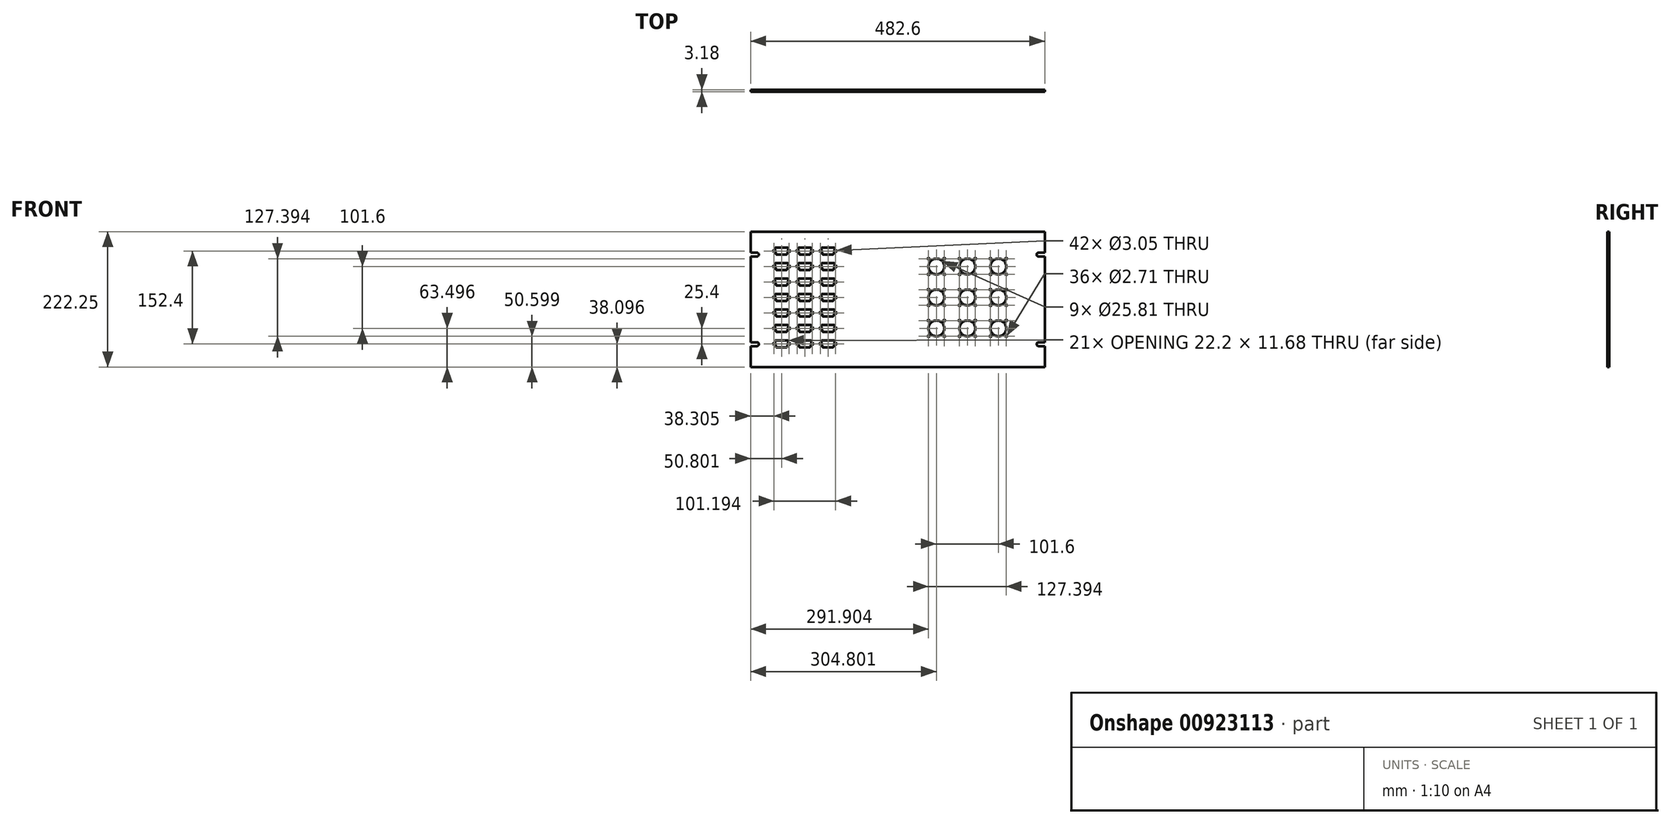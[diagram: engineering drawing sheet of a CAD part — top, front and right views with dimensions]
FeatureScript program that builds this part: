
annotation { "Feature Type Name" : "Feature", "Feature Type Description" : "" }
export const myFeature = defineFeature(function(context is Context, id is Id, definition is map)
    precondition{}
    {
        {
            var Q0;
            Q0=qCreatedBy(makeId("Front.planeOp"),FACE);
            var sketch = newSketch(context, id + "F0", { "sketchPlane" : qUnion([Q0])});
            skLineSegment(sketch, "E0.bottom", {"start": v(-256.05, -169.36) * mm, "end": v(226.55, -169.36) * mm});
            skLineSegment(sketch, "E0.top", {"start": v(-256.05, 52.89) * mm, "end": v(226.55, 52.89) * mm});
            skLineSegment(sketch, "E0.left", {"start": v(-256.05, -169.36) * mm, "end": v(-256.05, -134.95) * mm});
            skLineSegment(sketch, "E0.right", {"start": v(226.55, -169.36) * mm, "end": v(226.55, -134.95) * mm});
            skCircle(sketch, "E1", {"center": v(-217.75, -131.26) * mm, "radius": 1.52 * mm});
            skCircle(sketch, "E2", {"center": v(-192.75, -131.26) * mm, "radius": 1.52 * mm});
            skLineSegment(sketch, "E3", {"start": v(-217.75, -131.26) * mm, "end": v(-192.75, -131.26) * mm, "construction": true});
            skLineSegment(sketch, "E4", {"start": v(-205.25, -137.1) * mm, "end": v(-205.25, -125.42) * mm, "construction": true});
            skPoint(sketch, "E4.startSnap0", {"position": v(-205.25, -131.26) * mm});
            skLineSegment(sketch, "E5", {"start": v(-214.24, -125.42) * mm, "end": v(-196.26, -125.42) * mm});
            skLineSegment(sketch, "E6", {"start": v(-212.65, -137.1) * mm, "end": v(-197.84, -137.1) * mm});
            skLineSegment(sketch, "E7", {"start": v(-205.25, -125.42) * mm, "end": v(-205.25, -125.42) * mm});
            skLineSegment(sketch, "E8", {"start": v(-205.25, -137.1) * mm, "end": v(-205.25, -137.1) * mm});
            skArc(sketch, "E9", {"start": v(-214.24, -125.42) * mm, "mid": v(-215.88, -126.2) * mm, "end": v(-216.3, -127.97) * mm});
            skArc(sketch, "E10", {"start": v(-194.2, -127.97) * mm, "mid": v(-194.62, -126.2) * mm, "end": v(-196.26, -125.42) * mm});
            skArc(sketch, "E11", {"start": v(-197.84, -137.1) * mm, "mid": v(-196.52, -136.64) * mm, "end": v(-195.78, -135.44) * mm});
            skArc(sketch, "E12", {"start": v(-214.71, -135.44) * mm, "mid": v(-213.98, -136.64) * mm, "end": v(-212.65, -137.1) * mm});
            skPoint(sketch, "E13.orphan", {"position": v(-115.92, -125.42) * mm});
            skPoint(sketch, "E14.orphan", {"position": v(-123.87, -137.1) * mm});
            skLineSegment(sketch, "E15", {"start": v(-216.3, -127.97) * mm, "end": v(-214.71, -135.44) * mm});
            skLineSegment(sketch, "E16", {"start": v(-194.2, -127.97) * mm, "end": v(-195.78, -135.44) * mm});
            skPoint(sketch, "E17.0.1.0", {"position": v(-123.87, -111.7) * mm});
            skLineSegment(sketch, "E17.0.1.1", {"start": v(-216.3, -102.57) * mm, "end": v(-214.71, -110.04) * mm});
            skLineSegment(sketch, "E17.0.1.2", {"start": v(-194.2, -102.57) * mm, "end": v(-195.78, -110.04) * mm});
            skCircle(sketch, "E17.0.1.3", {"center": v(-192.75, -105.86) * mm, "radius": 1.52 * mm});
            skLineSegment(sketch, "E17.0.1.4", {"start": v(-214.24, -100.02) * mm, "end": v(-196.26, -100.02) * mm});
            skPoint(sketch, "E17.0.1.5", {"position": v(-205.25, -105.86) * mm});
            skPoint(sketch, "E17.0.1.6", {"position": v(-115.92, -100.02) * mm});
            skLineSegment(sketch, "E17.0.1.8", {"start": v(-212.65, -111.7) * mm, "end": v(-197.84, -111.7) * mm});
            skLineSegment(sketch, "E17.0.1.9", {"start": v(-217.75, -105.86) * mm, "end": v(-192.75, -105.86) * mm, "construction": true});
            skLineSegment(sketch, "E17.0.1.11", {"start": v(-205.25, -111.7) * mm, "end": v(-205.25, -100.02) * mm, "construction": true});
            skCircle(sketch, "E17.0.1.12", {"center": v(-217.75, -105.86) * mm, "radius": 1.52 * mm});
            skArc(sketch, "E17.0.1.13", {"start": v(-214.71, -110.04) * mm, "mid": v(-213.98, -111.24) * mm, "end": v(-212.65, -111.7) * mm});
            skArc(sketch, "E17.0.1.14", {"start": v(-214.24, -100.02) * mm, "mid": v(-215.88, -100.8) * mm, "end": v(-216.3, -102.57) * mm});
            skArc(sketch, "E17.0.1.15", {"start": v(-194.2, -102.57) * mm, "mid": v(-194.62, -100.8) * mm, "end": v(-196.26, -100.02) * mm});
            skArc(sketch, "E17.0.1.16", {"start": v(-197.84, -111.7) * mm, "mid": v(-196.52, -111.24) * mm, "end": v(-195.78, -110.04) * mm});
            skPoint(sketch, "E17.0.2.0", {"position": v(-123.87, -86.3) * mm});
            skLineSegment(sketch, "E17.0.2.1", {"start": v(-216.3, -77.17) * mm, "end": v(-214.71, -84.64) * mm});
            skLineSegment(sketch, "E17.0.2.2", {"start": v(-194.2, -77.17) * mm, "end": v(-195.78, -84.64) * mm});
            skCircle(sketch, "E17.0.2.3", {"center": v(-192.75, -80.46) * mm, "radius": 1.52 * mm});
            skLineSegment(sketch, "E17.0.2.4", {"start": v(-214.24, -74.62) * mm, "end": v(-196.26, -74.62) * mm});
            skPoint(sketch, "E17.0.2.5", {"position": v(-205.25, -80.46) * mm});
            skPoint(sketch, "E17.0.2.6", {"position": v(-115.92, -74.62) * mm});
            skLineSegment(sketch, "E17.0.2.8", {"start": v(-212.65, -86.3) * mm, "end": v(-197.84, -86.3) * mm});
            skLineSegment(sketch, "E17.0.2.9", {"start": v(-217.75, -80.46) * mm, "end": v(-192.75, -80.46) * mm, "construction": true});
            skLineSegment(sketch, "E17.0.2.11", {"start": v(-205.25, -86.3) * mm, "end": v(-205.25, -74.62) * mm, "construction": true});
            skCircle(sketch, "E17.0.2.12", {"center": v(-217.75, -80.46) * mm, "radius": 1.52 * mm});
            skArc(sketch, "E17.0.2.13", {"start": v(-214.71, -84.64) * mm, "mid": v(-213.98, -85.84) * mm, "end": v(-212.65, -86.3) * mm});
            skArc(sketch, "E17.0.2.14", {"start": v(-214.24, -74.62) * mm, "mid": v(-215.88, -75.4) * mm, "end": v(-216.3, -77.17) * mm});
            skArc(sketch, "E17.0.2.15", {"start": v(-194.2, -77.17) * mm, "mid": v(-194.62, -75.4) * mm, "end": v(-196.26, -74.62) * mm});
            skArc(sketch, "E17.0.2.16", {"start": v(-197.84, -86.3) * mm, "mid": v(-196.52, -85.84) * mm, "end": v(-195.78, -84.64) * mm});
            skPoint(sketch, "E17.0.3.0", {"position": v(-123.87, -60.9) * mm});
            skLineSegment(sketch, "E17.0.3.1", {"start": v(-216.3, -51.77) * mm, "end": v(-214.71, -59.24) * mm});
            skLineSegment(sketch, "E17.0.3.2", {"start": v(-194.2, -51.77) * mm, "end": v(-195.78, -59.24) * mm});
            skCircle(sketch, "E17.0.3.3", {"center": v(-192.75, -55.06) * mm, "radius": 1.52 * mm});
            skLineSegment(sketch, "E17.0.3.4", {"start": v(-214.24, -49.22) * mm, "end": v(-196.26, -49.22) * mm});
            skPoint(sketch, "E17.0.3.5", {"position": v(-205.25, -55.06) * mm});
            skPoint(sketch, "E17.0.3.6", {"position": v(-115.92, -49.22) * mm});
            skLineSegment(sketch, "E17.0.3.8", {"start": v(-212.65, -60.9) * mm, "end": v(-197.84, -60.9) * mm});
            skLineSegment(sketch, "E17.0.3.9", {"start": v(-217.75, -55.06) * mm, "end": v(-192.75, -55.06) * mm, "construction": true});
            skLineSegment(sketch, "E17.0.3.11", {"start": v(-205.25, -60.9) * mm, "end": v(-205.25, -49.22) * mm, "construction": true});
            skCircle(sketch, "E17.0.3.12", {"center": v(-217.75, -55.06) * mm, "radius": 1.52 * mm});
            skArc(sketch, "E17.0.3.13", {"start": v(-214.71, -59.24) * mm, "mid": v(-213.98, -60.44) * mm, "end": v(-212.65, -60.9) * mm});
            skArc(sketch, "E17.0.3.14", {"start": v(-214.24, -49.22) * mm, "mid": v(-215.88, -50) * mm, "end": v(-216.3, -51.77) * mm});
            skArc(sketch, "E17.0.3.15", {"start": v(-194.2, -51.77) * mm, "mid": v(-194.62, -50) * mm, "end": v(-196.26, -49.22) * mm});
            skArc(sketch, "E17.0.3.16", {"start": v(-197.84, -60.9) * mm, "mid": v(-196.52, -60.44) * mm, "end": v(-195.78, -59.24) * mm});
            skPoint(sketch, "E17.0.4.0", {"position": v(-123.87, -35.5) * mm});
            skLineSegment(sketch, "E17.0.4.1", {"start": v(-216.3, -26.37) * mm, "end": v(-214.71, -33.84) * mm});
            skLineSegment(sketch, "E17.0.4.2", {"start": v(-194.2, -26.37) * mm, "end": v(-195.78, -33.84) * mm});
            skCircle(sketch, "E17.0.4.3", {"center": v(-192.75, -29.66) * mm, "radius": 1.52 * mm});
            skLineSegment(sketch, "E17.0.4.4", {"start": v(-214.24, -23.82) * mm, "end": v(-196.26, -23.82) * mm});
            skPoint(sketch, "E17.0.4.5", {"position": v(-205.25, -29.66) * mm});
            skPoint(sketch, "E17.0.4.6", {"position": v(-115.92, -23.82) * mm});
            skLineSegment(sketch, "E17.0.4.8", {"start": v(-212.65, -35.5) * mm, "end": v(-197.84, -35.5) * mm});
            skLineSegment(sketch, "E17.0.4.9", {"start": v(-217.75, -29.66) * mm, "end": v(-192.75, -29.66) * mm, "construction": true});
            skLineSegment(sketch, "E17.0.4.11", {"start": v(-205.25, -35.5) * mm, "end": v(-205.25, -23.82) * mm, "construction": true});
            skCircle(sketch, "E17.0.4.12", {"center": v(-217.75, -29.66) * mm, "radius": 1.52 * mm});
            skArc(sketch, "E17.0.4.13", {"start": v(-214.71, -33.84) * mm, "mid": v(-213.98, -35.04) * mm, "end": v(-212.65, -35.5) * mm});
            skArc(sketch, "E17.0.4.14", {"start": v(-214.24, -23.82) * mm, "mid": v(-215.88, -24.6) * mm, "end": v(-216.3, -26.37) * mm});
            skArc(sketch, "E17.0.4.15", {"start": v(-194.2, -26.37) * mm, "mid": v(-194.62, -24.6) * mm, "end": v(-196.26, -23.82) * mm});
            skArc(sketch, "E17.0.4.16", {"start": v(-197.84, -35.5) * mm, "mid": v(-196.52, -35.04) * mm, "end": v(-195.78, -33.84) * mm});
            skPoint(sketch, "E17.0.5.0", {"position": v(-123.87, -10.1) * mm});
            skLineSegment(sketch, "E17.0.5.1", {"start": v(-216.3, -0.97) * mm, "end": v(-214.71, -8.44) * mm});
            skLineSegment(sketch, "E17.0.5.2", {"start": v(-194.2, -0.97) * mm, "end": v(-195.78, -8.44) * mm});
            skCircle(sketch, "E17.0.5.3", {"center": v(-192.75, -4.26) * mm, "radius": 1.52 * mm});
            skLineSegment(sketch, "E17.0.5.4", {"start": v(-214.24, 1.58) * mm, "end": v(-196.26, 1.58) * mm});
            skPoint(sketch, "E17.0.5.5", {"position": v(-205.25, -4.26) * mm});
            skPoint(sketch, "E17.0.5.6", {"position": v(-115.92, 1.58) * mm});
            skLineSegment(sketch, "E17.0.5.8", {"start": v(-212.65, -10.1) * mm, "end": v(-197.84, -10.1) * mm});
            skLineSegment(sketch, "E17.0.5.9", {"start": v(-217.75, -4.26) * mm, "end": v(-192.75, -4.26) * mm, "construction": true});
            skLineSegment(sketch, "E17.0.5.11", {"start": v(-205.25, -10.1) * mm, "end": v(-205.25, 1.58) * mm, "construction": true});
            skCircle(sketch, "E17.0.5.12", {"center": v(-217.75, -4.26) * mm, "radius": 1.52 * mm});
            skArc(sketch, "E17.0.5.13", {"start": v(-214.71, -8.44) * mm, "mid": v(-213.98, -9.64) * mm, "end": v(-212.65, -10.1) * mm});
            skArc(sketch, "E17.0.5.14", {"start": v(-214.24, 1.58) * mm, "mid": v(-215.88, 0.8) * mm, "end": v(-216.3, -0.97) * mm});
            skArc(sketch, "E17.0.5.15", {"start": v(-194.2, -0.97) * mm, "mid": v(-194.62, 0.8) * mm, "end": v(-196.26, 1.58) * mm});
            skArc(sketch, "E17.0.5.16", {"start": v(-197.84, -10.1) * mm, "mid": v(-196.52, -9.64) * mm, "end": v(-195.78, -8.44) * mm});
            skPoint(sketch, "E17.0.6.0", {"position": v(-123.87, 15.3) * mm});
            skLineSegment(sketch, "E17.0.6.1", {"start": v(-216.3, 24.43) * mm, "end": v(-214.71, 16.96) * mm});
            skLineSegment(sketch, "E17.0.6.2", {"start": v(-194.2, 24.43) * mm, "end": v(-195.78, 16.96) * mm});
            skCircle(sketch, "E17.0.6.3", {"center": v(-192.75, 21.14) * mm, "radius": 1.52 * mm});
            skLineSegment(sketch, "E17.0.6.4", {"start": v(-214.24, 26.98) * mm, "end": v(-196.26, 26.98) * mm});
            skPoint(sketch, "E17.0.6.5", {"position": v(-205.25, 21.14) * mm});
            skPoint(sketch, "E17.0.6.6", {"position": v(-115.92, 26.98) * mm});
            skLineSegment(sketch, "E17.0.6.8", {"start": v(-212.65, 15.3) * mm, "end": v(-197.84, 15.3) * mm});
            skLineSegment(sketch, "E17.0.6.9", {"start": v(-217.75, 21.14) * mm, "end": v(-192.75, 21.14) * mm, "construction": true});
            skLineSegment(sketch, "E17.0.6.11", {"start": v(-205.25, 15.3) * mm, "end": v(-205.25, 26.98) * mm, "construction": true});
            skCircle(sketch, "E17.0.6.12", {"center": v(-217.75, 21.14) * mm, "radius": 1.52 * mm});
            skArc(sketch, "E17.0.6.13", {"start": v(-214.71, 16.96) * mm, "mid": v(-213.98, 15.76) * mm, "end": v(-212.65, 15.3) * mm});
            skArc(sketch, "E17.0.6.14", {"start": v(-214.24, 26.98) * mm, "mid": v(-215.88, 26.2) * mm, "end": v(-216.3, 24.43) * mm});
            skArc(sketch, "E17.0.6.15", {"start": v(-194.2, 24.43) * mm, "mid": v(-194.62, 26.2) * mm, "end": v(-196.26, 26.98) * mm});
            skArc(sketch, "E17.0.6.16", {"start": v(-197.84, 15.3) * mm, "mid": v(-196.52, 15.76) * mm, "end": v(-195.78, 16.96) * mm});
            skLineSegment(sketch, "E17.1.0.1", {"start": v(-178.2, -127.97) * mm, "end": v(-176.61, -135.44) * mm});
            skLineSegment(sketch, "E17.1.0.2", {"start": v(-156.1, -127.97) * mm, "end": v(-157.68, -135.44) * mm});
            skCircle(sketch, "E17.1.0.3", {"center": v(-154.65, -131.26) * mm, "radius": 1.52 * mm});
            skLineSegment(sketch, "E17.1.0.4", {"start": v(-176.14, -125.42) * mm, "end": v(-158.16, -125.42) * mm});
            skPoint(sketch, "E17.1.0.5", {"position": v(-167.15, -131.26) * mm});
            skLineSegment(sketch, "E17.1.0.8", {"start": v(-174.55, -137.1) * mm, "end": v(-159.74, -137.1) * mm});
            skLineSegment(sketch, "E17.1.0.9", {"start": v(-179.65, -131.26) * mm, "end": v(-154.65, -131.26) * mm, "construction": true});
            skLineSegment(sketch, "E17.1.0.11", {"start": v(-167.15, -137.1) * mm, "end": v(-167.15, -125.42) * mm, "construction": true});
            skCircle(sketch, "E17.1.0.12", {"center": v(-179.65, -131.26) * mm, "radius": 1.52 * mm});
            skArc(sketch, "E17.1.0.13", {"start": v(-176.61, -135.44) * mm, "mid": v(-175.88, -136.64) * mm, "end": v(-174.55, -137.1) * mm});
            skArc(sketch, "E17.1.0.14", {"start": v(-176.14, -125.42) * mm, "mid": v(-177.78, -126.2) * mm, "end": v(-178.2, -127.97) * mm});
            skArc(sketch, "E17.1.0.15", {"start": v(-156.1, -127.97) * mm, "mid": v(-156.52, -126.2) * mm, "end": v(-158.16, -125.42) * mm});
            skArc(sketch, "E17.1.0.16", {"start": v(-159.74, -137.1) * mm, "mid": v(-158.42, -136.64) * mm, "end": v(-157.68, -135.44) * mm});
            skLineSegment(sketch, "E17.1.1.1", {"start": v(-178.2, -102.57) * mm, "end": v(-176.61, -110.04) * mm});
            skLineSegment(sketch, "E17.1.1.2", {"start": v(-156.1, -102.57) * mm, "end": v(-157.68, -110.04) * mm});
            skCircle(sketch, "E17.1.1.3", {"center": v(-154.65, -105.86) * mm, "radius": 1.52 * mm});
            skLineSegment(sketch, "E17.1.1.4", {"start": v(-176.14, -100.02) * mm, "end": v(-158.16, -100.02) * mm});
            skPoint(sketch, "E17.1.1.5", {"position": v(-167.15, -105.86) * mm});
            skLineSegment(sketch, "E17.1.1.8", {"start": v(-174.55, -111.7) * mm, "end": v(-159.74, -111.7) * mm});
            skLineSegment(sketch, "E17.1.1.9", {"start": v(-179.65, -105.86) * mm, "end": v(-154.65, -105.86) * mm, "construction": true});
            skLineSegment(sketch, "E17.1.1.11", {"start": v(-167.15, -111.7) * mm, "end": v(-167.15, -100.02) * mm, "construction": true});
            skCircle(sketch, "E17.1.1.12", {"center": v(-179.65, -105.86) * mm, "radius": 1.52 * mm});
            skArc(sketch, "E17.1.1.13", {"start": v(-176.61, -110.04) * mm, "mid": v(-175.88, -111.24) * mm, "end": v(-174.55, -111.7) * mm});
            skArc(sketch, "E17.1.1.14", {"start": v(-176.14, -100.02) * mm, "mid": v(-177.78, -100.8) * mm, "end": v(-178.2, -102.57) * mm});
            skArc(sketch, "E17.1.1.15", {"start": v(-156.1, -102.57) * mm, "mid": v(-156.52, -100.8) * mm, "end": v(-158.16, -100.02) * mm});
            skArc(sketch, "E17.1.1.16", {"start": v(-159.74, -111.7) * mm, "mid": v(-158.42, -111.24) * mm, "end": v(-157.68, -110.04) * mm});
            skLineSegment(sketch, "E17.1.2.1", {"start": v(-178.2, -77.17) * mm, "end": v(-176.61, -84.64) * mm});
            skLineSegment(sketch, "E17.1.2.2", {"start": v(-156.1, -77.17) * mm, "end": v(-157.68, -84.64) * mm});
            skCircle(sketch, "E17.1.2.3", {"center": v(-154.65, -80.46) * mm, "radius": 1.52 * mm});
            skLineSegment(sketch, "E17.1.2.4", {"start": v(-176.14, -74.62) * mm, "end": v(-158.16, -74.62) * mm});
            skPoint(sketch, "E17.1.2.5", {"position": v(-167.15, -80.46) * mm});
            skLineSegment(sketch, "E17.1.2.8", {"start": v(-174.55, -86.3) * mm, "end": v(-159.74, -86.3) * mm});
            skLineSegment(sketch, "E17.1.2.9", {"start": v(-179.65, -80.46) * mm, "end": v(-154.65, -80.46) * mm, "construction": true});
            skLineSegment(sketch, "E17.1.2.11", {"start": v(-167.15, -86.3) * mm, "end": v(-167.15, -74.62) * mm, "construction": true});
            skCircle(sketch, "E17.1.2.12", {"center": v(-179.65, -80.46) * mm, "radius": 1.52 * mm});
            skArc(sketch, "E17.1.2.13", {"start": v(-176.61, -84.64) * mm, "mid": v(-175.88, -85.84) * mm, "end": v(-174.55, -86.3) * mm});
            skArc(sketch, "E17.1.2.14", {"start": v(-176.14, -74.62) * mm, "mid": v(-177.78, -75.4) * mm, "end": v(-178.2, -77.17) * mm});
            skArc(sketch, "E17.1.2.15", {"start": v(-156.1, -77.17) * mm, "mid": v(-156.52, -75.4) * mm, "end": v(-158.16, -74.62) * mm});
            skArc(sketch, "E17.1.2.16", {"start": v(-159.74, -86.3) * mm, "mid": v(-158.42, -85.84) * mm, "end": v(-157.68, -84.64) * mm});
            skLineSegment(sketch, "E17.1.3.1", {"start": v(-178.2, -51.77) * mm, "end": v(-176.61, -59.24) * mm});
            skLineSegment(sketch, "E17.1.3.2", {"start": v(-156.1, -51.77) * mm, "end": v(-157.68, -59.24) * mm});
            skCircle(sketch, "E17.1.3.3", {"center": v(-154.65, -55.06) * mm, "radius": 1.52 * mm});
            skLineSegment(sketch, "E17.1.3.4", {"start": v(-176.14, -49.22) * mm, "end": v(-158.16, -49.22) * mm});
            skPoint(sketch, "E17.1.3.5", {"position": v(-167.15, -55.06) * mm});
            skLineSegment(sketch, "E17.1.3.8", {"start": v(-174.55, -60.9) * mm, "end": v(-159.74, -60.9) * mm});
            skLineSegment(sketch, "E17.1.3.9", {"start": v(-179.65, -55.06) * mm, "end": v(-154.65, -55.06) * mm, "construction": true});
            skLineSegment(sketch, "E17.1.3.11", {"start": v(-167.15, -60.9) * mm, "end": v(-167.15, -49.22) * mm, "construction": true});
            skCircle(sketch, "E17.1.3.12", {"center": v(-179.65, -55.06) * mm, "radius": 1.52 * mm});
            skArc(sketch, "E17.1.3.13", {"start": v(-176.61, -59.24) * mm, "mid": v(-175.88, -60.44) * mm, "end": v(-174.55, -60.9) * mm});
            skArc(sketch, "E17.1.3.14", {"start": v(-176.14, -49.22) * mm, "mid": v(-177.78, -50) * mm, "end": v(-178.2, -51.77) * mm});
            skArc(sketch, "E17.1.3.15", {"start": v(-156.1, -51.77) * mm, "mid": v(-156.52, -50) * mm, "end": v(-158.16, -49.22) * mm});
            skArc(sketch, "E17.1.3.16", {"start": v(-159.74, -60.9) * mm, "mid": v(-158.42, -60.44) * mm, "end": v(-157.68, -59.24) * mm});
            skLineSegment(sketch, "E17.1.4.1", {"start": v(-178.2, -26.37) * mm, "end": v(-176.61, -33.84) * mm});
            skLineSegment(sketch, "E17.1.4.2", {"start": v(-156.1, -26.37) * mm, "end": v(-157.68, -33.84) * mm});
            skCircle(sketch, "E17.1.4.3", {"center": v(-154.65, -29.66) * mm, "radius": 1.52 * mm});
            skLineSegment(sketch, "E17.1.4.4", {"start": v(-176.14, -23.82) * mm, "end": v(-158.16, -23.82) * mm});
            skPoint(sketch, "E17.1.4.5", {"position": v(-167.15, -29.66) * mm});
            skLineSegment(sketch, "E17.1.4.8", {"start": v(-174.55, -35.5) * mm, "end": v(-159.74, -35.5) * mm});
            skLineSegment(sketch, "E17.1.4.9", {"start": v(-179.65, -29.66) * mm, "end": v(-154.65, -29.66) * mm, "construction": true});
            skLineSegment(sketch, "E17.1.4.11", {"start": v(-167.15, -35.5) * mm, "end": v(-167.15, -23.82) * mm, "construction": true});
            skCircle(sketch, "E17.1.4.12", {"center": v(-179.65, -29.66) * mm, "radius": 1.52 * mm});
            skArc(sketch, "E17.1.4.13", {"start": v(-176.61, -33.84) * mm, "mid": v(-175.88, -35.04) * mm, "end": v(-174.55, -35.5) * mm});
            skArc(sketch, "E17.1.4.14", {"start": v(-176.14, -23.82) * mm, "mid": v(-177.78, -24.6) * mm, "end": v(-178.2, -26.37) * mm});
            skArc(sketch, "E17.1.4.15", {"start": v(-156.1, -26.37) * mm, "mid": v(-156.52, -24.6) * mm, "end": v(-158.16, -23.82) * mm});
            skArc(sketch, "E17.1.4.16", {"start": v(-159.74, -35.5) * mm, "mid": v(-158.42, -35.04) * mm, "end": v(-157.68, -33.84) * mm});
            skLineSegment(sketch, "E17.1.5.1", {"start": v(-178.2, -0.97) * mm, "end": v(-176.61, -8.44) * mm});
            skLineSegment(sketch, "E17.1.5.2", {"start": v(-156.1, -0.97) * mm, "end": v(-157.68, -8.44) * mm});
            skCircle(sketch, "E17.1.5.3", {"center": v(-154.65, -4.26) * mm, "radius": 1.52 * mm});
            skLineSegment(sketch, "E17.1.5.4", {"start": v(-176.14, 1.58) * mm, "end": v(-158.16, 1.58) * mm});
            skPoint(sketch, "E17.1.5.5", {"position": v(-167.15, -4.26) * mm});
            skLineSegment(sketch, "E17.1.5.8", {"start": v(-174.55, -10.1) * mm, "end": v(-159.74, -10.1) * mm});
            skLineSegment(sketch, "E17.1.5.9", {"start": v(-179.65, -4.26) * mm, "end": v(-154.65, -4.26) * mm, "construction": true});
            skLineSegment(sketch, "E17.1.5.11", {"start": v(-167.15, -10.1) * mm, "end": v(-167.15, 1.58) * mm, "construction": true});
            skCircle(sketch, "E17.1.5.12", {"center": v(-179.65, -4.26) * mm, "radius": 1.52 * mm});
            skArc(sketch, "E17.1.5.13", {"start": v(-176.61, -8.44) * mm, "mid": v(-175.88, -9.64) * mm, "end": v(-174.55, -10.1) * mm});
            skArc(sketch, "E17.1.5.14", {"start": v(-176.14, 1.58) * mm, "mid": v(-177.78, 0.8) * mm, "end": v(-178.2, -0.97) * mm});
            skArc(sketch, "E17.1.5.15", {"start": v(-156.1, -0.97) * mm, "mid": v(-156.52, 0.8) * mm, "end": v(-158.16, 1.58) * mm});
            skArc(sketch, "E17.1.5.16", {"start": v(-159.74, -10.1) * mm, "mid": v(-158.42, -9.64) * mm, "end": v(-157.68, -8.44) * mm});
            skLineSegment(sketch, "E17.1.6.1", {"start": v(-178.2, 24.43) * mm, "end": v(-176.61, 16.96) * mm});
            skLineSegment(sketch, "E17.1.6.2", {"start": v(-156.1, 24.43) * mm, "end": v(-157.68, 16.96) * mm});
            skCircle(sketch, "E17.1.6.3", {"center": v(-154.65, 21.14) * mm, "radius": 1.52 * mm});
            skLineSegment(sketch, "E17.1.6.4", {"start": v(-176.14, 26.98) * mm, "end": v(-158.16, 26.98) * mm});
            skPoint(sketch, "E17.1.6.5", {"position": v(-167.15, 21.14) * mm});
            skLineSegment(sketch, "E17.1.6.8", {"start": v(-174.55, 15.3) * mm, "end": v(-159.74, 15.3) * mm});
            skLineSegment(sketch, "E17.1.6.9", {"start": v(-179.65, 21.14) * mm, "end": v(-154.65, 21.14) * mm, "construction": true});
            skLineSegment(sketch, "E17.1.6.11", {"start": v(-167.15, 15.3) * mm, "end": v(-167.15, 26.98) * mm, "construction": true});
            skCircle(sketch, "E17.1.6.12", {"center": v(-179.65, 21.14) * mm, "radius": 1.52 * mm});
            skArc(sketch, "E17.1.6.13", {"start": v(-176.61, 16.96) * mm, "mid": v(-175.88, 15.76) * mm, "end": v(-174.55, 15.3) * mm});
            skArc(sketch, "E17.1.6.14", {"start": v(-176.14, 26.98) * mm, "mid": v(-177.78, 26.2) * mm, "end": v(-178.2, 24.43) * mm});
            skArc(sketch, "E17.1.6.15", {"start": v(-156.1, 24.43) * mm, "mid": v(-156.52, 26.2) * mm, "end": v(-158.16, 26.98) * mm});
            skArc(sketch, "E17.1.6.16", {"start": v(-159.74, 15.3) * mm, "mid": v(-158.42, 15.76) * mm, "end": v(-157.68, 16.96) * mm});
            skLineSegment(sketch, "E17.direction1", {"start": v(-214.71, -135.44) * mm, "end": v(-176.61, -135.44) * mm, "construction": true});
            skLineSegment(sketch, "E17.direction2", {"start": v(-214.71, -135.44) * mm, "end": v(-214.71, -110.04) * mm, "construction": true});
            skLineSegment(sketch, "E18.1.2.0", {"start": v(-140.1, -127.97) * mm, "end": v(-138.51, -135.44) * mm});
            skLineSegment(sketch, "E18.4.2.0", {"start": v(-118, -127.97) * mm, "end": v(-119.58, -135.44) * mm});
            skCircle(sketch, "E18.7.2.0", {"center": v(-116.55, -131.26) * mm, "radius": 1.52 * mm});
            skLineSegment(sketch, "E18.9.2.0", {"start": v(-138.04, -125.42) * mm, "end": v(-120.06, -125.42) * mm});
            skPoint(sketch, "E18.12.2.0", {"position": v(-129.05, -131.26) * mm});
            skPoint(sketch, "E18.14.2.0", {"position": v(-210.43, -137.1) * mm});
            skLineSegment(sketch, "E18.15.2.0", {"start": v(-136.45, -137.1) * mm, "end": v(-121.64, -137.1) * mm});
            skLineSegment(sketch, "E18.18.2.0", {"start": v(-141.55, -131.26) * mm, "end": v(-116.55, -131.26) * mm, "construction": true});
            skPoint(sketch, "E18.21.2.0", {"position": v(-218.37, -125.42) * mm});
            skLineSegment(sketch, "E18.22.2.0", {"start": v(-129.05, -137.1) * mm, "end": v(-129.05, -125.42) * mm, "construction": true});
            skCircle(sketch, "E18.25.2.0", {"center": v(-141.55, -131.26) * mm, "radius": 1.52 * mm});
            skArc(sketch, "E18.27.2.0", {"start": v(-138.51, -135.44) * mm, "mid": v(-137.78, -136.64) * mm, "end": v(-136.45, -137.1) * mm});
            skArc(sketch, "E18.31.2.0", {"start": v(-138.04, -125.42) * mm, "mid": v(-139.68, -126.2) * mm, "end": v(-140.1, -127.97) * mm});
            skArc(sketch, "E18.35.2.0", {"start": v(-118, -127.97) * mm, "mid": v(-118.42, -126.2) * mm, "end": v(-120.06, -125.42) * mm});
            skArc(sketch, "E18.39.2.0", {"start": v(-121.64, -137.1) * mm, "mid": v(-120.32, -136.64) * mm, "end": v(-119.58, -135.44) * mm});
            skLineSegment(sketch, "E18.1.2.1", {"start": v(-140.1, -102.57) * mm, "end": v(-138.51, -110.04) * mm});
            skLineSegment(sketch, "E18.4.2.1", {"start": v(-118, -102.57) * mm, "end": v(-119.58, -110.04) * mm});
            skCircle(sketch, "E18.7.2.1", {"center": v(-116.55, -105.86) * mm, "radius": 1.52 * mm});
            skLineSegment(sketch, "E18.9.2.1", {"start": v(-138.04, -100.02) * mm, "end": v(-120.06, -100.02) * mm});
            skPoint(sketch, "E18.12.2.1", {"position": v(-129.05, -105.86) * mm});
            skPoint(sketch, "E18.14.2.1", {"position": v(-210.43, -111.7) * mm});
            skLineSegment(sketch, "E18.15.2.1", {"start": v(-136.45, -111.7) * mm, "end": v(-121.64, -111.7) * mm});
            skLineSegment(sketch, "E18.18.2.1", {"start": v(-141.55, -105.86) * mm, "end": v(-116.55, -105.86) * mm, "construction": true});
            skPoint(sketch, "E18.21.2.1", {"position": v(-218.37, -100.02) * mm});
            skLineSegment(sketch, "E18.22.2.1", {"start": v(-129.05, -111.7) * mm, "end": v(-129.05, -100.02) * mm, "construction": true});
            skCircle(sketch, "E18.25.2.1", {"center": v(-141.55, -105.86) * mm, "radius": 1.52 * mm});
            skArc(sketch, "E18.27.2.1", {"start": v(-138.51, -110.04) * mm, "mid": v(-137.78, -111.24) * mm, "end": v(-136.45, -111.7) * mm});
            skArc(sketch, "E18.31.2.1", {"start": v(-138.04, -100.02) * mm, "mid": v(-139.68, -100.8) * mm, "end": v(-140.1, -102.57) * mm});
            skArc(sketch, "E18.35.2.1", {"start": v(-118, -102.57) * mm, "mid": v(-118.42, -100.8) * mm, "end": v(-120.06, -100.02) * mm});
            skArc(sketch, "E18.39.2.1", {"start": v(-121.64, -111.7) * mm, "mid": v(-120.32, -111.24) * mm, "end": v(-119.58, -110.04) * mm});
            skLineSegment(sketch, "E18.1.2.2", {"start": v(-140.1, -77.17) * mm, "end": v(-138.51, -84.64) * mm});
            skLineSegment(sketch, "E18.4.2.2", {"start": v(-118, -77.17) * mm, "end": v(-119.58, -84.64) * mm});
            skCircle(sketch, "E18.7.2.2", {"center": v(-116.55, -80.46) * mm, "radius": 1.52 * mm});
            skLineSegment(sketch, "E18.9.2.2", {"start": v(-138.04, -74.62) * mm, "end": v(-120.06, -74.62) * mm});
            skPoint(sketch, "E18.12.2.2", {"position": v(-129.05, -80.46) * mm});
            skPoint(sketch, "E18.14.2.2", {"position": v(-210.43, -86.3) * mm});
            skLineSegment(sketch, "E18.15.2.2", {"start": v(-136.45, -86.3) * mm, "end": v(-121.64, -86.3) * mm});
            skLineSegment(sketch, "E18.18.2.2", {"start": v(-141.55, -80.46) * mm, "end": v(-116.55, -80.46) * mm, "construction": true});
            skPoint(sketch, "E18.21.2.2", {"position": v(-218.37, -74.62) * mm});
            skLineSegment(sketch, "E18.22.2.2", {"start": v(-129.05, -86.3) * mm, "end": v(-129.05, -74.62) * mm, "construction": true});
            skCircle(sketch, "E18.25.2.2", {"center": v(-141.55, -80.46) * mm, "radius": 1.52 * mm});
            skArc(sketch, "E18.27.2.2", {"start": v(-138.51, -84.64) * mm, "mid": v(-137.78, -85.84) * mm, "end": v(-136.45, -86.3) * mm});
            skArc(sketch, "E18.31.2.2", {"start": v(-138.04, -74.62) * mm, "mid": v(-139.68, -75.4) * mm, "end": v(-140.1, -77.17) * mm});
            skArc(sketch, "E18.35.2.2", {"start": v(-118, -77.17) * mm, "mid": v(-118.42, -75.4) * mm, "end": v(-120.06, -74.62) * mm});
            skArc(sketch, "E18.39.2.2", {"start": v(-121.64, -86.3) * mm, "mid": v(-120.32, -85.84) * mm, "end": v(-119.58, -84.64) * mm});
            skLineSegment(sketch, "E18.1.2.3", {"start": v(-140.1, -51.77) * mm, "end": v(-138.51, -59.24) * mm});
            skLineSegment(sketch, "E18.4.2.3", {"start": v(-118, -51.77) * mm, "end": v(-119.58, -59.24) * mm});
            skCircle(sketch, "E18.7.2.3", {"center": v(-116.55, -55.06) * mm, "radius": 1.52 * mm});
            skLineSegment(sketch, "E18.9.2.3", {"start": v(-138.04, -49.22) * mm, "end": v(-120.06, -49.22) * mm});
            skPoint(sketch, "E18.12.2.3", {"position": v(-129.05, -55.06) * mm});
            skPoint(sketch, "E18.14.2.3", {"position": v(-210.43, -60.9) * mm});
            skLineSegment(sketch, "E18.15.2.3", {"start": v(-136.45, -60.9) * mm, "end": v(-121.64, -60.9) * mm});
            skLineSegment(sketch, "E18.18.2.3", {"start": v(-141.55, -55.06) * mm, "end": v(-116.55, -55.06) * mm, "construction": true});
            skPoint(sketch, "E18.21.2.3", {"position": v(-218.37, -49.22) * mm});
            skLineSegment(sketch, "E18.22.2.3", {"start": v(-129.05, -60.9) * mm, "end": v(-129.05, -49.22) * mm, "construction": true});
            skCircle(sketch, "E18.25.2.3", {"center": v(-141.55, -55.06) * mm, "radius": 1.52 * mm});
            skArc(sketch, "E18.27.2.3", {"start": v(-138.51, -59.24) * mm, "mid": v(-137.78, -60.44) * mm, "end": v(-136.45, -60.9) * mm});
            skArc(sketch, "E18.31.2.3", {"start": v(-138.04, -49.22) * mm, "mid": v(-139.68, -50) * mm, "end": v(-140.1, -51.77) * mm});
            skArc(sketch, "E18.35.2.3", {"start": v(-118, -51.77) * mm, "mid": v(-118.42, -50) * mm, "end": v(-120.06, -49.22) * mm});
            skArc(sketch, "E18.39.2.3", {"start": v(-121.64, -60.9) * mm, "mid": v(-120.32, -60.44) * mm, "end": v(-119.58, -59.24) * mm});
            skLineSegment(sketch, "E18.1.2.4", {"start": v(-140.1, -26.37) * mm, "end": v(-138.51, -33.84) * mm});
            skLineSegment(sketch, "E18.4.2.4", {"start": v(-118, -26.37) * mm, "end": v(-119.58, -33.84) * mm});
            skCircle(sketch, "E18.7.2.4", {"center": v(-116.55, -29.66) * mm, "radius": 1.52 * mm});
            skLineSegment(sketch, "E18.9.2.4", {"start": v(-138.04, -23.82) * mm, "end": v(-120.06, -23.82) * mm});
            skPoint(sketch, "E18.12.2.4", {"position": v(-129.05, -29.66) * mm});
            skPoint(sketch, "E18.14.2.4", {"position": v(-210.43, -35.5) * mm});
            skLineSegment(sketch, "E18.15.2.4", {"start": v(-136.45, -35.5) * mm, "end": v(-121.64, -35.5) * mm});
            skLineSegment(sketch, "E18.18.2.4", {"start": v(-141.55, -29.66) * mm, "end": v(-116.55, -29.66) * mm, "construction": true});
            skPoint(sketch, "E18.21.2.4", {"position": v(-218.37, -23.82) * mm});
            skLineSegment(sketch, "E18.22.2.4", {"start": v(-129.05, -35.5) * mm, "end": v(-129.05, -23.82) * mm, "construction": true});
            skCircle(sketch, "E18.25.2.4", {"center": v(-141.55, -29.66) * mm, "radius": 1.52 * mm});
            skArc(sketch, "E18.27.2.4", {"start": v(-138.51, -33.84) * mm, "mid": v(-137.78, -35.04) * mm, "end": v(-136.45, -35.5) * mm});
            skArc(sketch, "E18.31.2.4", {"start": v(-138.04, -23.82) * mm, "mid": v(-139.68, -24.6) * mm, "end": v(-140.1, -26.37) * mm});
            skArc(sketch, "E18.35.2.4", {"start": v(-118, -26.37) * mm, "mid": v(-118.42, -24.6) * mm, "end": v(-120.06, -23.82) * mm});
            skArc(sketch, "E18.39.2.4", {"start": v(-121.64, -35.5) * mm, "mid": v(-120.32, -35.04) * mm, "end": v(-119.58, -33.84) * mm});
            skLineSegment(sketch, "E18.1.2.5", {"start": v(-140.1, -0.97) * mm, "end": v(-138.51, -8.44) * mm});
            skLineSegment(sketch, "E18.4.2.5", {"start": v(-118, -0.97) * mm, "end": v(-119.58, -8.44) * mm});
            skCircle(sketch, "E18.7.2.5", {"center": v(-116.55, -4.26) * mm, "radius": 1.52 * mm});
            skLineSegment(sketch, "E18.9.2.5", {"start": v(-138.04, 1.58) * mm, "end": v(-120.06, 1.58) * mm});
            skPoint(sketch, "E18.12.2.5", {"position": v(-129.05, -4.26) * mm});
            skPoint(sketch, "E18.14.2.5", {"position": v(-210.43, -10.1) * mm});
            skLineSegment(sketch, "E18.15.2.5", {"start": v(-136.45, -10.1) * mm, "end": v(-121.64, -10.1) * mm});
            skLineSegment(sketch, "E18.18.2.5", {"start": v(-141.55, -4.26) * mm, "end": v(-116.55, -4.26) * mm, "construction": true});
            skPoint(sketch, "E18.21.2.5", {"position": v(-218.37, 1.58) * mm});
            skLineSegment(sketch, "E18.22.2.5", {"start": v(-129.05, -10.1) * mm, "end": v(-129.05, 1.58) * mm, "construction": true});
            skCircle(sketch, "E18.25.2.5", {"center": v(-141.55, -4.26) * mm, "radius": 1.52 * mm});
            skArc(sketch, "E18.27.2.5", {"start": v(-138.51, -8.44) * mm, "mid": v(-137.78, -9.64) * mm, "end": v(-136.45, -10.1) * mm});
            skArc(sketch, "E18.31.2.5", {"start": v(-138.04, 1.58) * mm, "mid": v(-139.68, 0.8) * mm, "end": v(-140.1, -0.97) * mm});
            skArc(sketch, "E18.35.2.5", {"start": v(-118, -0.97) * mm, "mid": v(-118.42, 0.8) * mm, "end": v(-120.06, 1.58) * mm});
            skArc(sketch, "E18.39.2.5", {"start": v(-121.64, -10.1) * mm, "mid": v(-120.32, -9.64) * mm, "end": v(-119.58, -8.44) * mm});
            skLineSegment(sketch, "E18.1.2.6", {"start": v(-140.1, 24.43) * mm, "end": v(-138.51, 16.96) * mm});
            skLineSegment(sketch, "E18.4.2.6", {"start": v(-118, 24.43) * mm, "end": v(-119.58, 16.96) * mm});
            skCircle(sketch, "E18.7.2.6", {"center": v(-116.55, 21.14) * mm, "radius": 1.52 * mm});
            skLineSegment(sketch, "E18.9.2.6", {"start": v(-138.04, 26.98) * mm, "end": v(-120.06, 26.98) * mm});
            skPoint(sketch, "E18.12.2.6", {"position": v(-129.05, 21.14) * mm});
            skPoint(sketch, "E18.14.2.6", {"position": v(-210.43, 15.3) * mm});
            skLineSegment(sketch, "E18.15.2.6", {"start": v(-136.45, 15.3) * mm, "end": v(-121.64, 15.3) * mm});
            skLineSegment(sketch, "E18.18.2.6", {"start": v(-141.55, 21.14) * mm, "end": v(-116.55, 21.14) * mm, "construction": true});
            skPoint(sketch, "E18.21.2.6", {"position": v(-218.37, 26.98) * mm});
            skLineSegment(sketch, "E18.22.2.6", {"start": v(-129.05, 15.3) * mm, "end": v(-129.05, 26.98) * mm, "construction": true});
            skCircle(sketch, "E18.25.2.6", {"center": v(-141.55, 21.14) * mm, "radius": 1.52 * mm});
            skArc(sketch, "E18.27.2.6", {"start": v(-138.51, 16.96) * mm, "mid": v(-137.78, 15.76) * mm, "end": v(-136.45, 15.3) * mm});
            skArc(sketch, "E18.31.2.6", {"start": v(-138.04, 26.98) * mm, "mid": v(-139.68, 26.2) * mm, "end": v(-140.1, 24.43) * mm});
            skArc(sketch, "E18.35.2.6", {"start": v(-118, 24.43) * mm, "mid": v(-118.42, 26.2) * mm, "end": v(-120.06, 26.98) * mm});
            skArc(sketch, "E18.39.2.6", {"start": v(-121.64, 15.3) * mm, "mid": v(-120.32, 15.76) * mm, "end": v(-119.58, 16.96) * mm});
            skLineSegment(sketch, "E19", {"start": v(48.75, -90.62) * mm, "end": v(48.75, -121.1) * mm, "construction": true});
            skLineSegment(sketch, "E20", {"start": v(61.45, -105.86) * mm, "end": v(48.75, -105.86) * mm, "construction": true});
            skArc(sketch, "E21", {"start": v(48.75, -92.96) * mm, "mid": v(35.85, -105.86) * mm, "end": v(48.75, -118.77) * mm});
            skPoint(sketch, "E22", {"position": v(36.44, -93.56) * mm});
            skPoint(sketch, "E23", {"position": v(35.26, -92.38) * mm});
            skLineSegment(sketch, "E24", {"start": v(35.26, -92.38) * mm, "end": v(36.44, -93.56) * mm, "construction": true});
            skPoint(sketch, "E25", {"position": v(35.85, -92.97) * mm});
            skPoint(sketch, "E26.MirrorP", {"position": v(61.65, -92.97) * mm});
            skArc(sketch, "E27.MirrorCS", {"start": v(48.75, -92.96) * mm, "mid": v(61.65, -105.86) * mm, "end": v(48.75, -118.77) * mm});
            skPoint(sketch, "E28.MirrorP", {"position": v(35.85, -118.76) * mm});
            skPoint(sketch, "E29.MirrorP", {"position": v(61.65, -118.76) * mm});
            skPoint(sketch, "E30.0.1.0", {"position": v(61.65, -42.17) * mm});
            skLineSegment(sketch, "E30.0.1.1", {"start": v(48.75, -39.82) * mm, "end": v(48.75, -70.3) * mm, "construction": true});
            skPoint(sketch, "E30.0.1.2", {"position": v(36.44, -42.76) * mm});
            skArc(sketch, "E30.0.1.3", {"start": v(48.75, -42.16) * mm, "mid": v(35.85, -55.06) * mm, "end": v(48.75, -67.97) * mm});
            skPoint(sketch, "E30.0.1.4", {"position": v(35.85, -42.17) * mm});
            skArc(sketch, "E30.0.1.5", {"start": v(48.75, -42.16) * mm, "mid": v(61.65, -55.06) * mm, "end": v(48.75, -67.97) * mm});
            skPoint(sketch, "E30.0.1.6", {"position": v(61.65, -67.96) * mm});
            skPoint(sketch, "E30.0.1.7", {"position": v(35.85, -67.96) * mm});
            skLineSegment(sketch, "E30.0.1.8", {"start": v(61.45, -55.06) * mm, "end": v(48.75, -55.06) * mm, "construction": true});
            skPoint(sketch, "E30.0.1.9", {"position": v(35.26, -41.58) * mm});
            skLineSegment(sketch, "E30.0.1.10", {"start": v(35.26, -41.58) * mm, "end": v(36.44, -42.76) * mm, "construction": true});
            skPoint(sketch, "E30.0.2.0", {"position": v(61.65, 8.63) * mm});
            skLineSegment(sketch, "E30.0.2.1", {"start": v(48.75, 10.98) * mm, "end": v(48.75, -19.5) * mm, "construction": true});
            skPoint(sketch, "E30.0.2.2", {"position": v(36.44, 8.04) * mm});
            skArc(sketch, "E30.0.2.3", {"start": v(48.75, 8.64) * mm, "mid": v(35.85, -4.26) * mm, "end": v(48.75, -17.17) * mm});
            skPoint(sketch, "E30.0.2.4", {"position": v(35.85, 8.63) * mm});
            skArc(sketch, "E30.0.2.5", {"start": v(48.75, 8.64) * mm, "mid": v(61.65, -4.26) * mm, "end": v(48.75, -17.17) * mm});
            skPoint(sketch, "E30.0.2.6", {"position": v(61.65, -17.16) * mm});
            skPoint(sketch, "E30.0.2.7", {"position": v(35.85, -17.16) * mm});
            skLineSegment(sketch, "E30.0.2.8", {"start": v(61.45, -4.26) * mm, "end": v(48.75, -4.26) * mm, "construction": true});
            skPoint(sketch, "E30.0.2.9", {"position": v(35.26, 9.22) * mm});
            skLineSegment(sketch, "E30.0.2.10", {"start": v(35.26, 9.22) * mm, "end": v(36.44, 8.04) * mm, "construction": true});
            skPoint(sketch, "E30.1.0.0", {"position": v(112.45, -92.97) * mm});
            skLineSegment(sketch, "E30.1.0.1", {"start": v(99.55, -90.62) * mm, "end": v(99.55, -121.1) * mm, "construction": true});
            skPoint(sketch, "E30.1.0.2", {"position": v(87.24, -93.56) * mm});
            skArc(sketch, "E30.1.0.3", {"start": v(99.55, -92.96) * mm, "mid": v(86.65, -105.86) * mm, "end": v(99.55, -118.77) * mm});
            skPoint(sketch, "E30.1.0.4", {"position": v(86.65, -92.97) * mm});
            skArc(sketch, "E30.1.0.5", {"start": v(99.55, -92.96) * mm, "mid": v(112.45, -105.86) * mm, "end": v(99.55, -118.77) * mm});
            skPoint(sketch, "E30.1.0.6", {"position": v(112.45, -118.76) * mm});
            skPoint(sketch, "E30.1.0.7", {"position": v(86.65, -118.76) * mm});
            skLineSegment(sketch, "E30.1.0.8", {"start": v(112.25, -105.86) * mm, "end": v(99.55, -105.86) * mm, "construction": true});
            skPoint(sketch, "E30.1.0.9", {"position": v(86.06, -92.38) * mm});
            skLineSegment(sketch, "E30.1.0.10", {"start": v(86.06, -92.38) * mm, "end": v(87.24, -93.56) * mm, "construction": true});
            skPoint(sketch, "E30.1.1.0", {"position": v(112.45, -42.17) * mm});
            skLineSegment(sketch, "E30.1.1.1", {"start": v(99.55, -39.82) * mm, "end": v(99.55, -70.3) * mm, "construction": true});
            skPoint(sketch, "E30.1.1.2", {"position": v(87.24, -42.76) * mm});
            skArc(sketch, "E30.1.1.3", {"start": v(99.55, -42.16) * mm, "mid": v(86.65, -55.06) * mm, "end": v(99.55, -67.97) * mm});
            skPoint(sketch, "E30.1.1.4", {"position": v(86.65, -42.17) * mm});
            skArc(sketch, "E30.1.1.5", {"start": v(99.55, -42.16) * mm, "mid": v(112.45, -55.06) * mm, "end": v(99.55, -67.97) * mm});
            skPoint(sketch, "E30.1.1.6", {"position": v(112.45, -67.96) * mm});
            skPoint(sketch, "E30.1.1.7", {"position": v(86.65, -67.96) * mm});
            skLineSegment(sketch, "E30.1.1.8", {"start": v(112.25, -55.06) * mm, "end": v(99.55, -55.06) * mm, "construction": true});
            skPoint(sketch, "E30.1.1.9", {"position": v(86.06, -41.58) * mm});
            skLineSegment(sketch, "E30.1.1.10", {"start": v(86.06, -41.58) * mm, "end": v(87.24, -42.76) * mm, "construction": true});
            skPoint(sketch, "E30.1.2.0", {"position": v(112.45, 8.63) * mm});
            skLineSegment(sketch, "E30.1.2.1", {"start": v(99.55, 10.98) * mm, "end": v(99.55, -19.5) * mm, "construction": true});
            skPoint(sketch, "E30.1.2.2", {"position": v(87.24, 8.04) * mm});
            skArc(sketch, "E30.1.2.3", {"start": v(99.55, 8.64) * mm, "mid": v(86.65, -4.26) * mm, "end": v(99.55, -17.17) * mm});
            skPoint(sketch, "E30.1.2.4", {"position": v(86.65, 8.63) * mm});
            skArc(sketch, "E30.1.2.5", {"start": v(99.55, 8.64) * mm, "mid": v(112.45, -4.26) * mm, "end": v(99.55, -17.17) * mm});
            skPoint(sketch, "E30.1.2.6", {"position": v(112.45, -17.16) * mm});
            skPoint(sketch, "E30.1.2.7", {"position": v(86.65, -17.16) * mm});
            skLineSegment(sketch, "E30.1.2.8", {"start": v(112.25, -4.26) * mm, "end": v(99.55, -4.26) * mm, "construction": true});
            skPoint(sketch, "E30.1.2.9", {"position": v(86.06, 9.22) * mm});
            skLineSegment(sketch, "E30.1.2.10", {"start": v(86.06, 9.22) * mm, "end": v(87.24, 8.04) * mm, "construction": true});
            skPoint(sketch, "E30.2.0.0", {"position": v(163.25, -92.97) * mm});
            skLineSegment(sketch, "E30.2.0.1", {"start": v(150.35, -90.62) * mm, "end": v(150.35, -121.1) * mm, "construction": true});
            skPoint(sketch, "E30.2.0.2", {"position": v(138.04, -93.56) * mm});
            skArc(sketch, "E30.2.0.3", {"start": v(150.35, -92.96) * mm, "mid": v(137.45, -105.86) * mm, "end": v(150.35, -118.77) * mm});
            skPoint(sketch, "E30.2.0.4", {"position": v(137.45, -92.97) * mm});
            skArc(sketch, "E30.2.0.5", {"start": v(150.35, -92.96) * mm, "mid": v(163.25, -105.86) * mm, "end": v(150.35, -118.77) * mm});
            skPoint(sketch, "E30.2.0.6", {"position": v(163.25, -118.76) * mm});
            skPoint(sketch, "E30.2.0.7", {"position": v(137.45, -118.76) * mm});
            skLineSegment(sketch, "E30.2.0.8", {"start": v(163.05, -105.86) * mm, "end": v(150.35, -105.86) * mm, "construction": true});
            skPoint(sketch, "E30.2.0.9", {"position": v(136.86, -92.38) * mm});
            skLineSegment(sketch, "E30.2.0.10", {"start": v(136.86, -92.38) * mm, "end": v(138.04, -93.56) * mm, "construction": true});
            skPoint(sketch, "E30.2.1.0", {"position": v(163.25, -42.17) * mm});
            skLineSegment(sketch, "E30.2.1.1", {"start": v(150.35, -39.82) * mm, "end": v(150.35, -70.3) * mm, "construction": true});
            skPoint(sketch, "E30.2.1.2", {"position": v(138.04, -42.76) * mm});
            skArc(sketch, "E30.2.1.3", {"start": v(150.35, -42.16) * mm, "mid": v(137.45, -55.06) * mm, "end": v(150.35, -67.97) * mm});
            skPoint(sketch, "E30.2.1.4", {"position": v(137.45, -42.17) * mm});
            skArc(sketch, "E30.2.1.5", {"start": v(150.35, -42.16) * mm, "mid": v(163.25, -55.06) * mm, "end": v(150.35, -67.97) * mm});
            skPoint(sketch, "E30.2.1.6", {"position": v(163.25, -67.96) * mm});
            skPoint(sketch, "E30.2.1.7", {"position": v(137.45, -67.96) * mm});
            skLineSegment(sketch, "E30.2.1.8", {"start": v(163.05, -55.06) * mm, "end": v(150.35, -55.06) * mm, "construction": true});
            skPoint(sketch, "E30.2.1.9", {"position": v(136.86, -41.58) * mm});
            skLineSegment(sketch, "E30.2.1.10", {"start": v(136.86, -41.58) * mm, "end": v(138.04, -42.76) * mm, "construction": true});
            skPoint(sketch, "E30.2.2.0", {"position": v(163.25, 8.63) * mm});
            skLineSegment(sketch, "E30.2.2.1", {"start": v(150.35, 10.98) * mm, "end": v(150.35, -19.5) * mm, "construction": true});
            skPoint(sketch, "E30.2.2.2", {"position": v(138.04, 8.04) * mm});
            skArc(sketch, "E30.2.2.3", {"start": v(150.35, 8.64) * mm, "mid": v(137.45, -4.26) * mm, "end": v(150.35, -17.17) * mm});
            skPoint(sketch, "E30.2.2.4", {"position": v(137.45, 8.63) * mm});
            skArc(sketch, "E30.2.2.5", {"start": v(150.35, 8.64) * mm, "mid": v(163.25, -4.26) * mm, "end": v(150.35, -17.17) * mm});
            skPoint(sketch, "E30.2.2.6", {"position": v(163.25, -17.16) * mm});
            skPoint(sketch, "E30.2.2.7", {"position": v(137.45, -17.16) * mm});
            skLineSegment(sketch, "E30.2.2.8", {"start": v(163.05, -4.26) * mm, "end": v(150.35, -4.26) * mm, "construction": true});
            skPoint(sketch, "E30.2.2.9", {"position": v(136.86, 9.22) * mm});
            skLineSegment(sketch, "E30.2.2.10", {"start": v(136.86, 9.22) * mm, "end": v(138.04, 8.04) * mm, "construction": true});
            skLineSegment(sketch, "E30.direction1", {"start": v(35.85, -118.76) * mm, "end": v(86.65, -118.76) * mm, "construction": true});
            skLineSegment(sketch, "E30.direction2", {"start": v(35.85, -118.76) * mm, "end": v(35.85, -67.96) * mm, "construction": true});
            skPoint(sketch, "E31", {"position": v(-245.76, 15.3) * mm});
            skLineSegment(sketch, "E32", {"start": v(-256.05, -58.24) * mm, "end": v(-239.44, -58.24) * mm, "construction": true});
            skLineSegment(sketch, "E33", {"start": v(-14.75, 52.89) * mm, "end": v(-14.75, 38.2) * mm, "construction": true});
            skLineSegment(sketch, "E34", {"start": v(-245.76, 15.3) * mm, "end": v(-256.05, 15.3) * mm, "construction": true});
            skArc(sketch, "E35.0.startCap", {"start": v(-245.76, 18.47) * mm, "mid": v(-242.59, 15.3) * mm, "end": v(-245.76, 12.12) * mm});
            skLineSegment(sketch, "E35.0.left", {"start": v(-245.76, 12.12) * mm, "end": v(-256.05, 12.12) * mm});
            skLineSegment(sketch, "E35.0.right", {"start": v(-245.76, 18.47) * mm, "end": v(-256.05, 18.47) * mm});
            skLineSegment(sketch, "E36.trimOffspring", {"start": v(-256.05, 18.47) * mm, "end": v(-256.05, 52.89) * mm});
            skArc(sketch, "E37.MirrorCS", {"start": v(-245.76, -134.95) * mm, "mid": v(-242.59, -131.77) * mm, "end": v(-245.76, -128.6) * mm});
            skLineSegment(sketch, "E38.MirrorCS", {"start": v(-245.76, -128.6) * mm, "end": v(-256.05, -128.6) * mm});
            skLineSegment(sketch, "E39.MirrorCS", {"start": v(-256.05, -134.95) * mm, "end": v(-256.05, -169.36) * mm});
            skLineSegment(sketch, "E40.MirrorCS", {"start": v(-245.76, -134.95) * mm, "end": v(-256.05, -134.95) * mm});
            skLineSegment(sketch, "E41.trimOffspring", {"start": v(-256.05, -128.6) * mm, "end": v(-256.05, 12.12) * mm});
            skArc(sketch, "E42.MirrorCS", {"start": v(216.26, 18.47) * mm, "mid": v(213.09, 15.3) * mm, "end": v(216.26, 12.12) * mm});
            skLineSegment(sketch, "E43.MirrorCS", {"start": v(216.26, 12.12) * mm, "end": v(226.55, 12.12) * mm});
            skLineSegment(sketch, "E44.MirrorCS", {"start": v(216.26, 18.47) * mm, "end": v(226.55, 18.47) * mm});
            skLineSegment(sketch, "E45.MirrorCS", {"start": v(216.26, -128.6) * mm, "end": v(226.55, -128.6) * mm});
            skArc(sketch, "E46.MirrorCS", {"start": v(216.26, -134.95) * mm, "mid": v(213.09, -131.77) * mm, "end": v(216.26, -128.6) * mm});
            skLineSegment(sketch, "E47.MirrorCS", {"start": v(216.26, -134.95) * mm, "end": v(226.55, -134.95) * mm});
            skLineSegment(sketch, "E48.trimOffspring", {"start": v(226.55, 18.47) * mm, "end": v(226.55, 52.89) * mm});
            skLineSegment(sketch, "E49.trimOffspring", {"start": v(226.55, -128.6) * mm, "end": v(226.55, 12.12) * mm});
            skSolve(sketch);
        }
        {
            var Q0;
            Q0 = qSketchRegion(id + "F0", true);
            extrude(context, id + "F1", {"entities" : qUnion([Q0]), "depth" : 3.17 * mm, "offsetDistance" : 25.4 * mm});
        }
        {
            var Q0;
            Q0=sQuery(id+"F0.wireOp",VERTEX,"E30.0.2.4");
            var Q1;
            Q1=sQuery(id+"F0.wireOp",VERTEX,"E30.0.2.0");
            var Q2;
            Q2=sQuery(id+"F0.wireOp",VERTEX,"E30.0.2.6");
            var Q3;
            Q3=sQuery(id+"F0.wireOp",VERTEX,"E30.0.2.7");
            var Q4;
            Q4=sQuery(id+"F0.wireOp",VERTEX,"E30.1.2.7");
            var Q5;
            Q5=sQuery(id+"F0.wireOp",VERTEX,"E30.1.2.6");
            var Q6;
            Q6=sQuery(id+"F0.wireOp",VERTEX,"E30.1.2.0");
            var Q7;
            Q7=sQuery(id+"F0.wireOp",VERTEX,"E30.1.2.4");
            var Q8;
            Q8=sQuery(id+"F0.wireOp",VERTEX,"E30.0.1.4");
            var Q9;
            Q9=sQuery(id+"F0.wireOp",VERTEX,"E30.0.1.0");
            var Q10;
            Q10=sQuery(id+"F0.wireOp",VERTEX,"E30.1.1.4");
            var Q11;
            Q11=sQuery(id+"F0.wireOp",VERTEX,"E30.1.1.0");
            var Q12;
            Q12=sQuery(id+"F0.wireOp",VERTEX,"E30.2.2.4");
            var Q13;
            Q13=sQuery(id+"F0.wireOp",VERTEX,"E30.2.2.0");
            var Q14;
            Q14=sQuery(id+"F0.wireOp",VERTEX,"E30.2.2.6");
            var Q15;
            Q15=sQuery(id+"F0.wireOp",VERTEX,"E30.2.2.7");
            var Q16;
            Q16=sQuery(id+"F0.wireOp",VERTEX,"E30.2.1.4");
            var Q17;
            Q17=sQuery(id+"F0.wireOp",VERTEX,"E30.2.1.0");
            var Q18;
            Q18=sQuery(id+"F0.wireOp",VERTEX,"E30.0.1.7");
            var Q19;
            Q19=sQuery(id+"F0.wireOp",VERTEX,"E30.0.1.6");
            var Q20;
            Q20=sQuery(id+"F0.wireOp",VERTEX,"E30.1.1.7");
            var Q21;
            Q21=sQuery(id+"F0.wireOp",VERTEX,"E30.1.1.6");
            var Q22;
            Q22=sQuery(id+"F0.wireOp",VERTEX,"E30.2.1.7");
            var Q23;
            Q23=sQuery(id+"F0.wireOp",VERTEX,"E30.2.1.6");
            var Q24;
            Q24=sQuery(id+"F0.wireOp",VERTEX,"E30.2.0.0");
            var Q25;
            Q25=sQuery(id+"F0.wireOp",VERTEX,"E30.2.0.4");
            var Q26;
            Q26=sQuery(id+"F0.wireOp",VERTEX,"E30.1.0.0");
            var Q27;
            Q27=sQuery(id+"F0.wireOp",VERTEX,"E30.1.0.4");
            var Q28;
            Q28=sQuery(id+"F0.wireOp",VERTEX,"E26.MirrorP");
            var Q29;
            Q29=sQuery(id+"F0.wireOp",VERTEX,"E25");
            var Q30;
            Q30=sQuery(id+"F0.wireOp",VERTEX,"E28.MirrorP");
            var Q31;
            Q31=sQuery(id+"F0.wireOp",VERTEX,"E29.MirrorP");
            var Q32;
            Q32=sQuery(id+"F0.wireOp",VERTEX,"E30.1.0.7");
            var Q33;
            Q33=sQuery(id+"F0.wireOp",VERTEX,"E30.1.0.6");
            var Q34;
            Q34=sQuery(id+"F0.wireOp",VERTEX,"E30.2.0.7");
            var Q35;
            Q35=sQuery(id+"F0.wireOp",VERTEX,"E30.2.0.6");
            var Q36;
            Q36=makeQuery(id+"F1.opExtrude","SWEPT_BODY",BODY,{"disambiguationData":[OSD([sQuery(id+"F0.wireOp",EDGE,"E0.bottom"),sQuery(id+"F0.wireOp",EDGE,"E0.top"),sQuery(id+"F0.wireOp",EDGE,"E0.left"),sQuery(id+"F0.wireOp",EDGE,"E0.right"),sQuery(id+"F0.wireOp",EDGE,"E1"),sQuery(id+"F0.wireOp",EDGE,"E2"),sQuery(id+"F0.wireOp",EDGE,"E5"),sQuery(id+"F0.wireOp",EDGE,"E6"),sQuery(id+"F0.wireOp",EDGE,"E9"),sQuery(id+"F0.wireOp",EDGE,"E10"),sQuery(id+"F0.wireOp",EDGE,"E11"),sQuery(id+"F0.wireOp",EDGE,"E12"),sQuery(id+"F0.wireOp",EDGE,"E15"),sQuery(id+"F0.wireOp",EDGE,"E16"),sQuery(id+"F0.wireOp",EDGE,"E17.0.1.1"),sQuery(id+"F0.wireOp",EDGE,"E17.0.1.2"),sQuery(id+"F0.wireOp",EDGE,"E17.0.1.3"),sQuery(id+"F0.wireOp",EDGE,"E17.0.1.4"),sQuery(id+"F0.wireOp",EDGE,"E17.0.1.8"),sQuery(id+"F0.wireOp",EDGE,"E17.0.1.12"),sQuery(id+"F0.wireOp",EDGE,"E17.0.1.13"),sQuery(id+"F0.wireOp",EDGE,"E17.0.1.14"),sQuery(id+"F0.wireOp",EDGE,"E17.0.1.15"),sQuery(id+"F0.wireOp",EDGE,"E17.0.1.16"),sQuery(id+"F0.wireOp",EDGE,"E17.0.2.1"),sQuery(id+"F0.wireOp",EDGE,"E17.0.2.2"),sQuery(id+"F0.wireOp",EDGE,"E17.0.2.3"),sQuery(id+"F0.wireOp",EDGE,"E17.0.2.4"),sQuery(id+"F0.wireOp",EDGE,"E17.0.2.8"),sQuery(id+"F0.wireOp",EDGE,"E17.0.2.12"),sQuery(id+"F0.wireOp",EDGE,"E17.0.2.13"),sQuery(id+"F0.wireOp",EDGE,"E17.0.2.14"),sQuery(id+"F0.wireOp",EDGE,"E17.0.2.15"),sQuery(id+"F0.wireOp",EDGE,"E17.0.2.16"),sQuery(id+"F0.wireOp",EDGE,"E17.0.3.1"),sQuery(id+"F0.wireOp",EDGE,"E17.0.3.2"),sQuery(id+"F0.wireOp",EDGE,"E17.0.3.3"),sQuery(id+"F0.wireOp",EDGE,"E17.0.3.4"),sQuery(id+"F0.wireOp",EDGE,"E17.0.3.8"),sQuery(id+"F0.wireOp",EDGE,"E17.0.3.12"),sQuery(id+"F0.wireOp",EDGE,"E17.0.3.13"),sQuery(id+"F0.wireOp",EDGE,"E17.0.3.14"),sQuery(id+"F0.wireOp",EDGE,"E17.0.3.15"),sQuery(id+"F0.wireOp",EDGE,"E17.0.3.16"),sQuery(id+"F0.wireOp",EDGE,"E17.0.4.1"),sQuery(id+"F0.wireOp",EDGE,"E17.0.4.2"),sQuery(id+"F0.wireOp",EDGE,"E17.0.4.3"),sQuery(id+"F0.wireOp",EDGE,"E17.0.4.4"),sQuery(id+"F0.wireOp",EDGE,"E17.0.4.8"),sQuery(id+"F0.wireOp",EDGE,"E17.0.4.12"),sQuery(id+"F0.wireOp",EDGE,"E17.0.4.13"),sQuery(id+"F0.wireOp",EDGE,"E17.0.4.14"),sQuery(id+"F0.wireOp",EDGE,"E17.0.4.15"),sQuery(id+"F0.wireOp",EDGE,"E17.0.4.16"),sQuery(id+"F0.wireOp",EDGE,"E17.0.5.1"),sQuery(id+"F0.wireOp",EDGE,"E17.0.5.2"),sQuery(id+"F0.wireOp",EDGE,"E17.0.5.3"),sQuery(id+"F0.wireOp",EDGE,"E17.0.5.4"),sQuery(id+"F0.wireOp",EDGE,"E17.0.5.8"),sQuery(id+"F0.wireOp",EDGE,"E17.0.5.12"),sQuery(id+"F0.wireOp",EDGE,"E17.0.5.13"),sQuery(id+"F0.wireOp",EDGE,"E17.0.5.14"),sQuery(id+"F0.wireOp",EDGE,"E17.0.5.15"),sQuery(id+"F0.wireOp",EDGE,"E17.0.5.16"),sQuery(id+"F0.wireOp",EDGE,"E17.0.6.1"),sQuery(id+"F0.wireOp",EDGE,"E17.0.6.2"),sQuery(id+"F0.wireOp",EDGE,"E17.0.6.3"),sQuery(id+"F0.wireOp",EDGE,"E17.0.6.4"),sQuery(id+"F0.wireOp",EDGE,"E17.0.6.8"),sQuery(id+"F0.wireOp",EDGE,"E17.0.6.12"),sQuery(id+"F0.wireOp",EDGE,"E17.0.6.13"),sQuery(id+"F0.wireOp",EDGE,"E17.0.6.14"),sQuery(id+"F0.wireOp",EDGE,"E17.0.6.15"),sQuery(id+"F0.wireOp",EDGE,"E17.0.6.16"),sQuery(id+"F0.wireOp",EDGE,"E17.1.0.1"),sQuery(id+"F0.wireOp",EDGE,"E17.1.0.2"),sQuery(id+"F0.wireOp",EDGE,"E17.1.0.3"),sQuery(id+"F0.wireOp",EDGE,"E17.1.0.4"),sQuery(id+"F0.wireOp",EDGE,"E17.1.0.8"),sQuery(id+"F0.wireOp",EDGE,"E17.1.0.12"),sQuery(id+"F0.wireOp",EDGE,"E17.1.0.13"),sQuery(id+"F0.wireOp",EDGE,"E17.1.0.14"),sQuery(id+"F0.wireOp",EDGE,"E17.1.0.15"),sQuery(id+"F0.wireOp",EDGE,"E17.1.0.16"),sQuery(id+"F0.wireOp",EDGE,"E17.1.1.1"),sQuery(id+"F0.wireOp",EDGE,"E17.1.1.2"),sQuery(id+"F0.wireOp",EDGE,"E17.1.1.3"),sQuery(id+"F0.wireOp",EDGE,"E17.1.1.4"),sQuery(id+"F0.wireOp",EDGE,"E17.1.1.8"),sQuery(id+"F0.wireOp",EDGE,"E17.1.1.12"),sQuery(id+"F0.wireOp",EDGE,"E17.1.1.13"),sQuery(id+"F0.wireOp",EDGE,"E17.1.1.14"),sQuery(id+"F0.wireOp",EDGE,"E17.1.1.15"),sQuery(id+"F0.wireOp",EDGE,"E17.1.1.16"),sQuery(id+"F0.wireOp",EDGE,"E17.1.2.1"),sQuery(id+"F0.wireOp",EDGE,"E17.1.2.2"),sQuery(id+"F0.wireOp",EDGE,"E17.1.2.3"),sQuery(id+"F0.wireOp",EDGE,"E17.1.2.4"),sQuery(id+"F0.wireOp",EDGE,"E17.1.2.8"),sQuery(id+"F0.wireOp",EDGE,"E17.1.2.12"),sQuery(id+"F0.wireOp",EDGE,"E17.1.2.13"),sQuery(id+"F0.wireOp",EDGE,"E17.1.2.14"),sQuery(id+"F0.wireOp",EDGE,"E17.1.2.15"),sQuery(id+"F0.wireOp",EDGE,"E17.1.2.16"),sQuery(id+"F0.wireOp",EDGE,"E17.1.3.1"),sQuery(id+"F0.wireOp",EDGE,"E17.1.3.2"),sQuery(id+"F0.wireOp",EDGE,"E17.1.3.3"),sQuery(id+"F0.wireOp",EDGE,"E17.1.3.4"),sQuery(id+"F0.wireOp",EDGE,"E17.1.3.8"),sQuery(id+"F0.wireOp",EDGE,"E17.1.3.12"),sQuery(id+"F0.wireOp",EDGE,"E17.1.3.13"),sQuery(id+"F0.wireOp",EDGE,"E17.1.3.14"),sQuery(id+"F0.wireOp",EDGE,"E17.1.3.15"),sQuery(id+"F0.wireOp",EDGE,"E17.1.3.16"),sQuery(id+"F0.wireOp",EDGE,"E17.1.4.1"),sQuery(id+"F0.wireOp",EDGE,"E17.1.4.2"),sQuery(id+"F0.wireOp",EDGE,"E17.1.4.3"),sQuery(id+"F0.wireOp",EDGE,"E17.1.4.4"),sQuery(id+"F0.wireOp",EDGE,"E17.1.4.8"),sQuery(id+"F0.wireOp",EDGE,"E17.1.4.12"),sQuery(id+"F0.wireOp",EDGE,"E17.1.4.13"),sQuery(id+"F0.wireOp",EDGE,"E17.1.4.14"),sQuery(id+"F0.wireOp",EDGE,"E17.1.4.15"),sQuery(id+"F0.wireOp",EDGE,"E17.1.4.16"),sQuery(id+"F0.wireOp",EDGE,"E17.1.5.1"),sQuery(id+"F0.wireOp",EDGE,"E17.1.5.2"),sQuery(id+"F0.wireOp",EDGE,"E17.1.5.3"),sQuery(id+"F0.wireOp",EDGE,"E17.1.5.4"),sQuery(id+"F0.wireOp",EDGE,"E17.1.5.8"),sQuery(id+"F0.wireOp",EDGE,"E17.1.5.12"),sQuery(id+"F0.wireOp",EDGE,"E17.1.5.13"),sQuery(id+"F0.wireOp",EDGE,"E17.1.5.14"),sQuery(id+"F0.wireOp",EDGE,"E17.1.5.15"),sQuery(id+"F0.wireOp",EDGE,"E17.1.5.16"),sQuery(id+"F0.wireOp",EDGE,"E17.1.6.1"),sQuery(id+"F0.wireOp",EDGE,"E17.1.6.2"),sQuery(id+"F0.wireOp",EDGE,"E17.1.6.3"),sQuery(id+"F0.wireOp",EDGE,"E17.1.6.4"),sQuery(id+"F0.wireOp",EDGE,"E17.1.6.8"),sQuery(id+"F0.wireOp",EDGE,"E17.1.6.12"),sQuery(id+"F0.wireOp",EDGE,"E17.1.6.13"),sQuery(id+"F0.wireOp",EDGE,"E17.1.6.14"),sQuery(id+"F0.wireOp",EDGE,"E17.1.6.15"),sQuery(id+"F0.wireOp",EDGE,"E17.1.6.16"),sQuery(id+"F0.wireOp",EDGE,"E18.1.2.0"),sQuery(id+"F0.wireOp",EDGE,"E18.4.2.0"),sQuery(id+"F0.wireOp",EDGE,"E18.7.2.0"),sQuery(id+"F0.wireOp",EDGE,"E18.9.2.0"),sQuery(id+"F0.wireOp",EDGE,"E18.15.2.0"),sQuery(id+"F0.wireOp",EDGE,"E18.25.2.0"),sQuery(id+"F0.wireOp",EDGE,"E18.27.2.0"),sQuery(id+"F0.wireOp",EDGE,"E18.31.2.0"),sQuery(id+"F0.wireOp",EDGE,"E18.35.2.0"),sQuery(id+"F0.wireOp",EDGE,"E18.39.2.0"),sQuery(id+"F0.wireOp",EDGE,"E18.1.2.1"),sQuery(id+"F0.wireOp",EDGE,"E18.4.2.1"),sQuery(id+"F0.wireOp",EDGE,"E18.7.2.1"),sQuery(id+"F0.wireOp",EDGE,"E18.9.2.1"),sQuery(id+"F0.wireOp",EDGE,"E18.15.2.1"),sQuery(id+"F0.wireOp",EDGE,"E18.25.2.1"),sQuery(id+"F0.wireOp",EDGE,"E18.27.2.1"),sQuery(id+"F0.wireOp",EDGE,"E18.31.2.1"),sQuery(id+"F0.wireOp",EDGE,"E18.35.2.1"),sQuery(id+"F0.wireOp",EDGE,"E18.39.2.1"),sQuery(id+"F0.wireOp",EDGE,"E18.1.2.2"),sQuery(id+"F0.wireOp",EDGE,"E18.4.2.2"),sQuery(id+"F0.wireOp",EDGE,"E18.7.2.2"),sQuery(id+"F0.wireOp",EDGE,"E18.9.2.2"),sQuery(id+"F0.wireOp",EDGE,"E18.15.2.2"),sQuery(id+"F0.wireOp",EDGE,"E18.25.2.2"),sQuery(id+"F0.wireOp",EDGE,"E18.27.2.2"),sQuery(id+"F0.wireOp",EDGE,"E18.31.2.2"),sQuery(id+"F0.wireOp",EDGE,"E18.35.2.2"),sQuery(id+"F0.wireOp",EDGE,"E18.39.2.2"),sQuery(id+"F0.wireOp",EDGE,"E18.1.2.3"),sQuery(id+"F0.wireOp",EDGE,"E18.4.2.3"),sQuery(id+"F0.wireOp",EDGE,"E18.7.2.3"),sQuery(id+"F0.wireOp",EDGE,"E18.9.2.3"),sQuery(id+"F0.wireOp",EDGE,"E18.15.2.3"),sQuery(id+"F0.wireOp",EDGE,"E18.25.2.3"),sQuery(id+"F0.wireOp",EDGE,"E18.27.2.3"),sQuery(id+"F0.wireOp",EDGE,"E18.31.2.3"),sQuery(id+"F0.wireOp",EDGE,"E18.35.2.3"),sQuery(id+"F0.wireOp",EDGE,"E18.39.2.3"),sQuery(id+"F0.wireOp",EDGE,"E18.1.2.4"),sQuery(id+"F0.wireOp",EDGE,"E18.4.2.4"),sQuery(id+"F0.wireOp",EDGE,"E18.7.2.4"),sQuery(id+"F0.wireOp",EDGE,"E18.9.2.4"),sQuery(id+"F0.wireOp",EDGE,"E18.15.2.4"),sQuery(id+"F0.wireOp",EDGE,"E18.25.2.4"),sQuery(id+"F0.wireOp",EDGE,"E18.27.2.4"),sQuery(id+"F0.wireOp",EDGE,"E18.31.2.4"),sQuery(id+"F0.wireOp",EDGE,"E18.35.2.4"),sQuery(id+"F0.wireOp",EDGE,"E18.39.2.4"),sQuery(id+"F0.wireOp",EDGE,"E18.1.2.5"),sQuery(id+"F0.wireOp",EDGE,"E18.4.2.5"),sQuery(id+"F0.wireOp",EDGE,"E18.7.2.5"),sQuery(id+"F0.wireOp",EDGE,"E18.9.2.5"),sQuery(id+"F0.wireOp",EDGE,"E18.15.2.5"),sQuery(id+"F0.wireOp",EDGE,"E18.25.2.5"),sQuery(id+"F0.wireOp",EDGE,"E18.27.2.5"),sQuery(id+"F0.wireOp",EDGE,"E18.31.2.5"),sQuery(id+"F0.wireOp",EDGE,"E18.35.2.5"),sQuery(id+"F0.wireOp",EDGE,"E18.39.2.5"),sQuery(id+"F0.wireOp",EDGE,"E18.1.2.6"),sQuery(id+"F0.wireOp",EDGE,"E18.4.2.6"),sQuery(id+"F0.wireOp",EDGE,"E18.7.2.6"),sQuery(id+"F0.wireOp",EDGE,"E18.9.2.6"),sQuery(id+"F0.wireOp",EDGE,"E18.15.2.6"),sQuery(id+"F0.wireOp",EDGE,"E18.25.2.6"),sQuery(id+"F0.wireOp",EDGE,"E18.27.2.6"),sQuery(id+"F0.wireOp",EDGE,"E18.31.2.6"),sQuery(id+"F0.wireOp",EDGE,"E18.35.2.6"),sQuery(id+"F0.wireOp",EDGE,"E18.39.2.6"),sQuery(id+"F0.wireOp",EDGE,"E21"),sQuery(id+"F0.wireOp",EDGE,"E27.MirrorCS"),sQuery(id+"F0.wireOp",EDGE,"E30.0.1.3"),sQuery(id+"F0.wireOp",EDGE,"E30.0.1.5"),sQuery(id+"F0.wireOp",EDGE,"E30.0.2.3"),sQuery(id+"F0.wireOp",EDGE,"E30.0.2.5"),sQuery(id+"F0.wireOp",EDGE,"E30.1.0.3"),sQuery(id+"F0.wireOp",EDGE,"E30.1.0.5"),sQuery(id+"F0.wireOp",EDGE,"E30.1.1.3"),sQuery(id+"F0.wireOp",EDGE,"E30.1.1.5"),sQuery(id+"F0.wireOp",EDGE,"E30.1.2.3"),sQuery(id+"F0.wireOp",EDGE,"E30.1.2.5"),sQuery(id+"F0.wireOp",EDGE,"E30.2.0.3"),sQuery(id+"F0.wireOp",EDGE,"E30.2.0.5"),sQuery(id+"F0.wireOp",EDGE,"E30.2.1.3"),sQuery(id+"F0.wireOp",EDGE,"E30.2.1.5"),sQuery(id+"F0.wireOp",EDGE,"E30.2.2.3"),sQuery(id+"F0.wireOp",EDGE,"E30.2.2.5")])]});
            hole(context, id + "F2", {"style" : HoleStyle.SIMPLE, "endStyle" : HoleEndStyle.THROUGH, "oppositeDirection" : true, "standardTappedOrClearance" : lookupTablePath({ "standard" : "ANSI", "engagement" : "75%", "pitch" : "32 tpi", "size" : "#6", "type" : "Tapped" }), "standardBlindInLast" : lookupTablePath({ "standard" : "ANSI", "engagement" : "75%", "pitch" : "32 tpi", "size" : "#6", "type" : "Tapped" }), "holeDiameter" : 2.7 * mm, "majorDiameter" : 3.5 * mm, "showTappedDepth" : true, "isTappedThrough" : true, "tappedDepth" : 12.7 * mm, "tapClearance" : 3, "locations" : qUnion([Q0, Q1, Q2, Q3, Q4, Q5, Q6, Q7, Q8, Q9, Q10, Q11, Q12, Q13, Q14, Q15, Q16, Q17, Q18, Q19, Q20, Q21, Q22, Q23, Q24, Q25, Q26, Q27, Q28, Q29, Q30, Q31, Q32, Q33, Q34, Q35]), "scope" : qUnion([Q36])});
        }
    });
